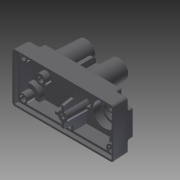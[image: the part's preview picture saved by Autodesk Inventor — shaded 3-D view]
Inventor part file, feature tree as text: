
AUTODESK INVENTOR PART (.ipt)
format: ipt  version: 2013 (Build 170138000, 138)  size: 545,792 bytes
history: native  units: in
note: dims shown in document units (in); Inventor stores cm internally (conversion verified against a paired STEP export)
features: sketch x19, extrude x17, fillet x7, mirror x4, hole x3, projected_geometry x3, plane x2, pattern_circular x1
ambient origin geometry x8: Origin, YZ Plane, XZ Plane, XY Plane, X Axis, Y Axis, Z Axis, Center Point
bodies: Solid1 (feature_tree)
feature tree (56):
  extrude  "Extrusion1"  Depth=0.059in TaperAngle=0.0deg
  extrude  "Extrusion3"  Depth=0.079in TaperAngle=0.0deg
  extrude  "Extrusion4"  Depth=0.059in TaperAngle=0.0deg
  sketch  "Sketch2"  dims[d7=0.197in d8=0.0in d9=0.079in d10=0.0in]
  extrude  "Extrusion5"  Depth=0.051in
  plane  "Work Plane1"
  plane  "Work Plane2"
  mirror  "Mirror1"
  mirror  "Mirror2"
  extrude  "Extrusion6"  Depth=0.1945in TaperAngle=0.0deg
  extrude  "Extrusion7"  Depth=0.132in TaperAngle=0.0deg
  sketch  "Sketch8"  dims[d33=0.0687in d34=0.346in d35=0.0in]
  extrude  "Extrusion9"  Depth=0.039in
  fillet  "Fillet3"  Radius=0.346in
  extrude  "Extrusion10"  Depth=0.346in TaperAngle=0.0deg
  extrude  "Extrusion11"  Depth=0.0687in
  extrude  "Extrusion12"  Depth=0.0687in
  extrude  "Extrusion13"  Depth=0.079in
  extrude  "Extrusion14"  Depth=0.334in
  pattern_circular  "Circular Pattern1"  [2 undecoded]
  extrude  "Extrusion15"  Depth=0.02in
  extrude  "Extrusion16"  Depth=0.02in
  extrude  "Extrusion17"  Depth=0.0395in
  hole  "Hole1"  [1 undecoded]
  hole  "Hole2"  [1 undecoded]
  sketch  "Sketch18"  dims[d67=0.02in]
  extrude  "Extrusion18"  [1 undecoded]
  extrude  "Extrusion19"  [1 undecoded]
  fillet  "Fillet4"  [1 undecoded]
  fillet  "Fillet5"  [1 undecoded]
  hole  "Hole3"  [1 undecoded]
  mirror  "Mirror3"
  mirror  "Mirror4"
  fillet  "Fillet6"  [1 undecoded]
  fillet  "Fillet8"  [1 undecoded]
  fillet  "Fillet9"  [1 undecoded]
  fillet  "Fillet7"  [1 undecoded]
  sketch  "Sketch1"  dims[d0=0.315in d1=-0.0103in d5=0.059in d6=0.0in]
  sketch  "Sketch3"  dims[d12=0.087in d13=0.0in d14=0.059in d15=0.0in]
  sketch  "Sketch4"  dims[d18=0.413in d19=0.051in d20=-0.0687in]
  sketch  "Sketch5"  dims[d21=0.02in d22=0.1945in d23=0.0in]
  projected_geometry  "Projected Loop1"
  sketch  "Sketch6"  dims[d24=0.28in d25=0.132in d26=0.0in]
  sketch  "Sketch7"  dims[d27=0.346in d28=-0.0069in d30=0.039in d31=0.346in d32=0.0in]
  sketch  "Sketch9"  dims[d36=1.1811in d37=180.0deg d39=0.0687in]
  sketch  "Sketch10"  dims[d40=0.346in d41=0.0in d42=0.0687in]
  sketch  "Sketch11"  dims[d43=0.346in d44=0.0in]
  sketch  "Sketch12"  dims[d45=0.087in d46=0.75in d47=0.375in d48=0.25in d49=0.5635in d50=1.0in d51=0.8108in]
  projected_geometry  "Projected Loop2"
  sketch  "Sketch13"  dims[d52=0.061in d53=0.75in d54=0.375in d55=0.25in d56=0.5635in d57=0.346in d58=0.0in d59=0.079in d60=0.0103in]
  sketch  "Sketch14"  dims[d61=0.334in d62=0.334in]
  sketch  "Sketch15"  dims[d63=0.284in]
  sketch  "Sketch16"  dims[d64=0.284in]
  sketch  "Sketch17"  dims[d65=0.598in d66=-0.0172in]
  sketch  "Sketch19"  dims[d68=0.472in d69=0.0in d70=0.058in d71=0.236in d72=0.75in d73=0.375in d74=0.25in d75=0.5635in d76=0.598in d77=0.0in d78=0.02in d79=0.02in d80=0.0395in d81=0.02in]
  projected_geometry  "Projected Loop3"
note: 13 required parameter values undecoded (feature->parameter linkage not recoverable at this tier; creation-order binding heuristic only, values carry confidence <= 0.55)
